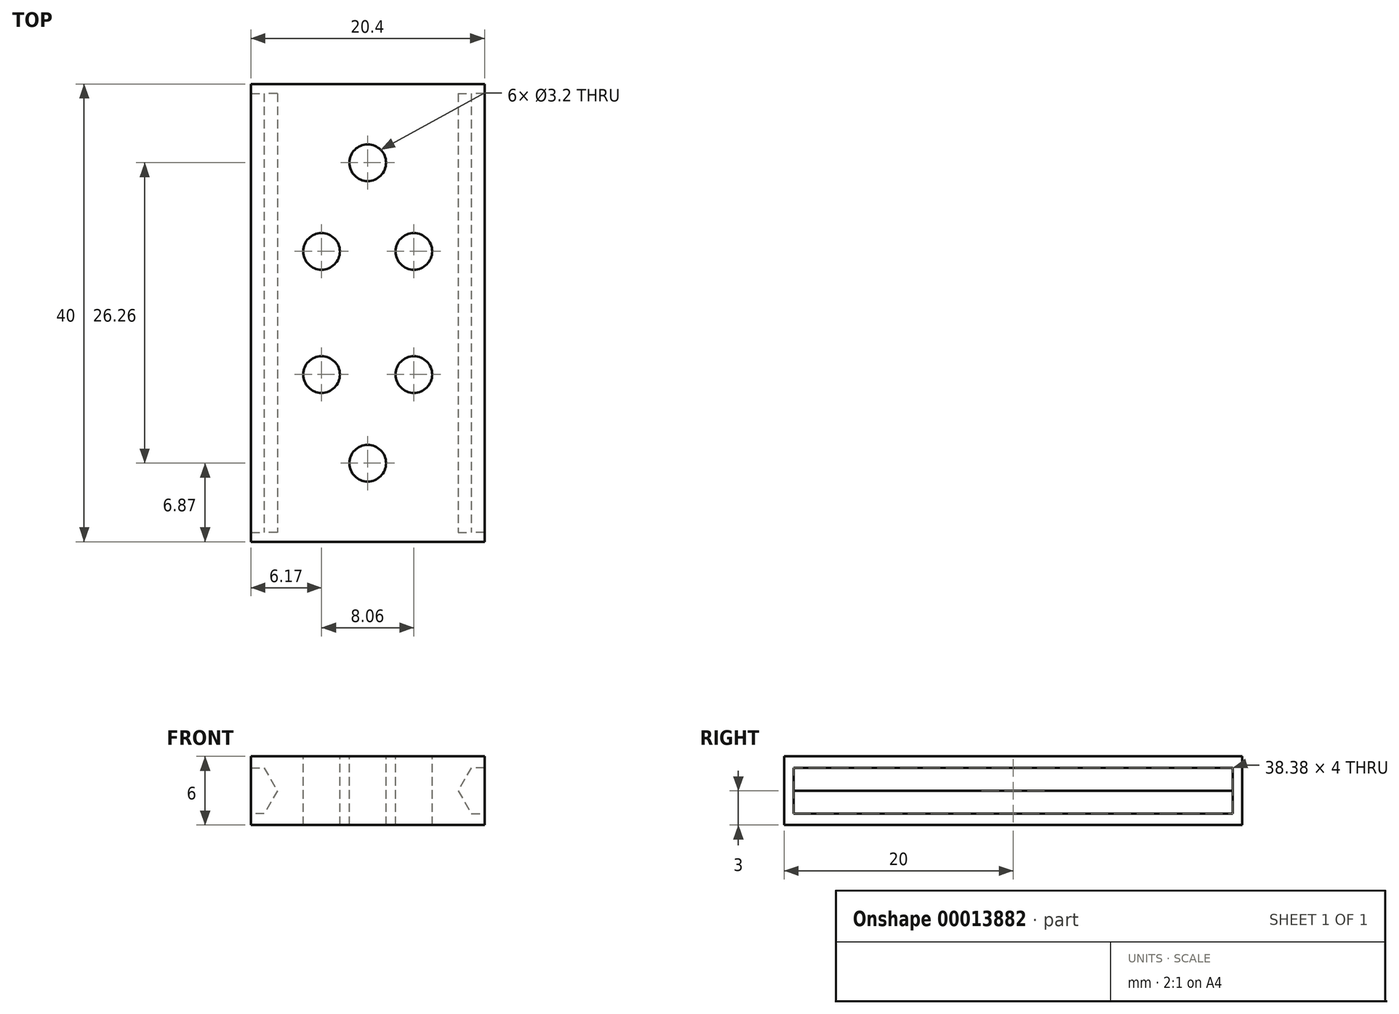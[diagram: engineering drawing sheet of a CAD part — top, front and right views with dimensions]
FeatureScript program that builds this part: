
annotation { "Feature Type Name" : "Feature", "Feature Type Description" : "" }
export const myFeature = defineFeature(function(context is Context, id is Id, definition is map)
    precondition{}
    {
        {
            var Q0;
            Q0=qCreatedBy(makeId("Top.planeOp"),FACE);
            var sketch = newSketch(context, id + "F0", { "sketchPlane" : qUnion([Q0])});
            skLineSegment(sketch, "E0.rect.bottom", {"start": v(-10.2, 10) * mm, "end": v(10.2, 10) * mm});
            skLineSegment(sketch, "E0.rect.top", {"start": v(-10.2, -10) * mm, "end": v(10.2, -10) * mm});
            skLineSegment(sketch, "E0.rect.left", {"start": v(-10.2, 10) * mm, "end": v(-10.2, -10) * mm});
            skLineSegment(sketch, "E0.rect.right", {"start": v(10.2, 10) * mm, "end": v(10.2, -10) * mm});
            skPoint(sketch, "E0.rect.middle", {"position": v(0, 0) * mm});
            skLineSegment(sketch, "E1", {"start": v(0, 10) * mm, "end": v(0, -10) * mm});
            skSolve(sketch);
        }
        {
            var Q0;
            {var subQ1=sQuery(id+"F0.wireOp",EDGE,"E0.rect.left");Q0=makeQuery(id+"F0.imprint","IMPRINT",FACE,{"disambiguationData":[TD([[makeQuery(id+"F0.imprint","IMPRINT",EDGE,{"derivedFrom":subQ1}),1.0]])]});}
            extrude(context, id + "F1", {"entities" : qUnion([Q0]), "endBound" : BoundingType.SYMMETRIC, "depth" : 6 * mm});
        }
        {
            var Q0;
            Q0=makeQuery(id+"F1.opExtrude","SWEPT_FACE",FACE,{"disambiguationData":[OSD([sQuery(id+"F0.wireOp",EDGE,"E0.rect.top")])]});
            var sketch = newSketch(context, id + "F2", { "sketchPlane" : qUnion([Q0])});
            skLineSegment(sketch, "E2", {"start": v(-10.2, 0) * mm, "end": v(0, 0) * mm});
            skCircle(sketch, "E3.cCircle", {"center": v(-10.2, 0) * mm, "radius": 2 * mm, "construction": true});
            skLineSegment(sketch, "E3.0", {"start": v(-9.05, -2) * mm, "end": v(-11.35, -2) * mm});
            skLineSegment(sketch, "E3.1", {"start": v(-11.35, -2) * mm, "end": v(-12.5, 0) * mm});
            skLineSegment(sketch, "E3.2", {"start": v(-12.5, 0) * mm, "end": v(-11.35, 2) * mm});
            skLineSegment(sketch, "E3.3", {"start": v(-11.35, 2) * mm, "end": v(-9.05, 2) * mm});
            skLineSegment(sketch, "E3.4", {"start": v(-9.05, 2) * mm, "end": v(-7.9, 0) * mm});
            skLineSegment(sketch, "E3.5", {"start": v(-7.9, 0) * mm, "end": v(-9.05, -2) * mm});
            skPoint(sketch, "E3.0.midPoint", {"position": v(-10.2, -2) * mm});
            skLineSegment(sketch, "E4", {"start": v(-9.05, 2) * mm, "end": v(-9.2, 2.27) * mm});
            skLineSegment(sketch, "E5", {"start": v(-9.2, 2.27) * mm, "end": v(-10.2, 2.27) * mm});
            skLineSegment(sketch, "E6.MirrorCS", {"start": v(-9.2, -2.27) * mm, "end": v(-10.2, -2.27) * mm});
            skLineSegment(sketch, "E7.MirrorCS", {"start": v(-9.05, -2) * mm, "end": v(-9.2, -2.27) * mm});
            skSolve(sketch);
        }
        {
            var Q0;
            {var subQ5=sQuery(id+"F2.wireOp",EDGE,"E3.5");Q0=makeQuery(id+"F2.imprint","IMPRINT",FACE,{"disambiguationData":[TD([[makeQuery(id+"F2.imprint","IMPRINT",EDGE,{"derivedFrom":subQ5}),-1.0]])]});}
            var Q1;
            {var subQ5=sQuery(id+"F2.wireOp",EDGE,"E3.4");Q1=makeQuery(id+"F2.imprint","IMPRINT",FACE,{"disambiguationData":[TD([[makeQuery(id+"F2.imprint","IMPRINT",EDGE,{"derivedFrom":subQ5}),-1.0]])]});}
            extrude(context, id + "F3", {"entities" : qUnion([Q0, Q1]), "operationType" : NewBodyOperationType.REMOVE, "oppositeDirection" : true, "depth" : 19.2 * mm});
        }
        {
            var Q0;
            Q0=makeQuery(id+"F1.opExtrude","SWEPT_BODY",BODY,{"disambiguationData":[OSD([sQuery(id+"F0.wireOp",EDGE,"E0.rect.bottom"),sQuery(id+"F0.wireOp",EDGE,"E0.rect.top"),sQuery(id+"F0.wireOp",EDGE,"E0.rect.left"),sQuery(id+"F0.wireOp",EDGE,"E1")])]});
            var Q1;
            Q1=makeQuery(id+"F1.opExtrude","SWEPT_FACE",FACE,{"disambiguationData":[OSD([sQuery(id+"F0.wireOp",EDGE,"E1")])]});
            mirror(context, id + "F4", {"operationType" : NewBodyOperationType.ADD, "entities" : qUnion([Q0]), "mirrorPlane" : qUnion([Q1])});
        }
        {
            var Q0;
            Q0=makeQuery(id+"F1.opExtrude","SWEPT_BODY",BODY,{"disambiguationData":[OSD([sQuery(id+"F0.wireOp",EDGE,"E0.rect.bottom"),sQuery(id+"F0.wireOp",EDGE,"E0.rect.top"),sQuery(id+"F0.wireOp",EDGE,"E0.rect.left"),sQuery(id+"F0.wireOp",EDGE,"E1")])]});
            var Q1;
            {var subQ0=makeQuery(id+"F1.opExtrude","SWEPT_FACE",FACE,{"disambiguationData":[OSD([sQuery(id+"F0.wireOp",EDGE,"E0.rect.top")])]});Q1=makeQuery(id+"F4.boolean.opBoolean","MERGE",FACE,{"derivedFrom":[subQ0,makeQuery(id+"F4.opPattern","COPY",FACE,{"derivedFrom":subQ0,"instanceName":"1"})]});}
            mirror(context, id + "F5", {"operationType" : NewBodyOperationType.ADD, "entities" : qUnion([Q0]), "mirrorPlane" : qUnion([Q1])});
        }
        {
            var Q0;
            {var subQ0=makeQuery(id+"F1.opExtrude","CAP_FACE",FACE,{"disambiguationData":[OSD([sQuery(id+"F0.wireOp",EDGE,"E0.rect.bottom"),sQuery(id+"F0.wireOp",EDGE,"E0.rect.top"),sQuery(id+"F0.wireOp",EDGE,"E0.rect.left"),sQuery(id+"F0.wireOp",EDGE,"E1")])],"isStart":false});var subQ1=makeQuery(id+"F4.boolean.opBoolean","MERGE",FACE,{"derivedFrom":[subQ0,makeQuery(id+"F4.opPattern","COPY",FACE,{"derivedFrom":subQ0,"instanceName":"1"})]});Q0=makeQuery(id+"F5.boolean.opBoolean","MERGE",FACE,{"derivedFrom":[subQ1,makeQuery(id+"F5.opPattern","COPY",FACE,{"derivedFrom":subQ1,"instanceName":"1"})]});}
            var sketch = newSketch(context, id + "F6", { "sketchPlane" : qUnion([Q0])});
            skLineSegment(sketch, "E8", {"start": v(0, 10) * mm, "end": v(0, -30) * mm, "construction": true});
            skCircle(sketch, "E9", {"center": v(0, 3.13) * mm, "radius": 1.6 * mm});
            skLineSegment(sketch, "E10", {"start": v(10.2, -10) * mm, "end": v(-10.2, -10) * mm, "construction": true});
            skCircle(sketch, "E11", {"center": v(4.03, -4.62) * mm, "radius": 1.6 * mm});
            skCircle(sketch, "E12.MirrorC", {"center": v(-4.03, -4.62) * mm, "radius": 1.6 * mm});
            skCircle(sketch, "E13.MirrorC", {"center": v(4.03, -15.38) * mm, "radius": 1.6 * mm});
            skCircle(sketch, "E14.MirrorC", {"center": v(-4.03, -15.38) * mm, "radius": 1.6 * mm});
            skCircle(sketch, "E15.MirrorC", {"center": v(0, -23.13) * mm, "radius": 1.6 * mm});
            skSolve(sketch);
        }
        {
            var Q0;
            Q0 = qSketchRegion(id + "F6", true);
            extrude(context, id + "F7", {"entities" : qUnion([Q0]), "operationType" : NewBodyOperationType.REMOVE, "oppositeDirection" : true, "depth" : 25 * mm});
        }
    });
